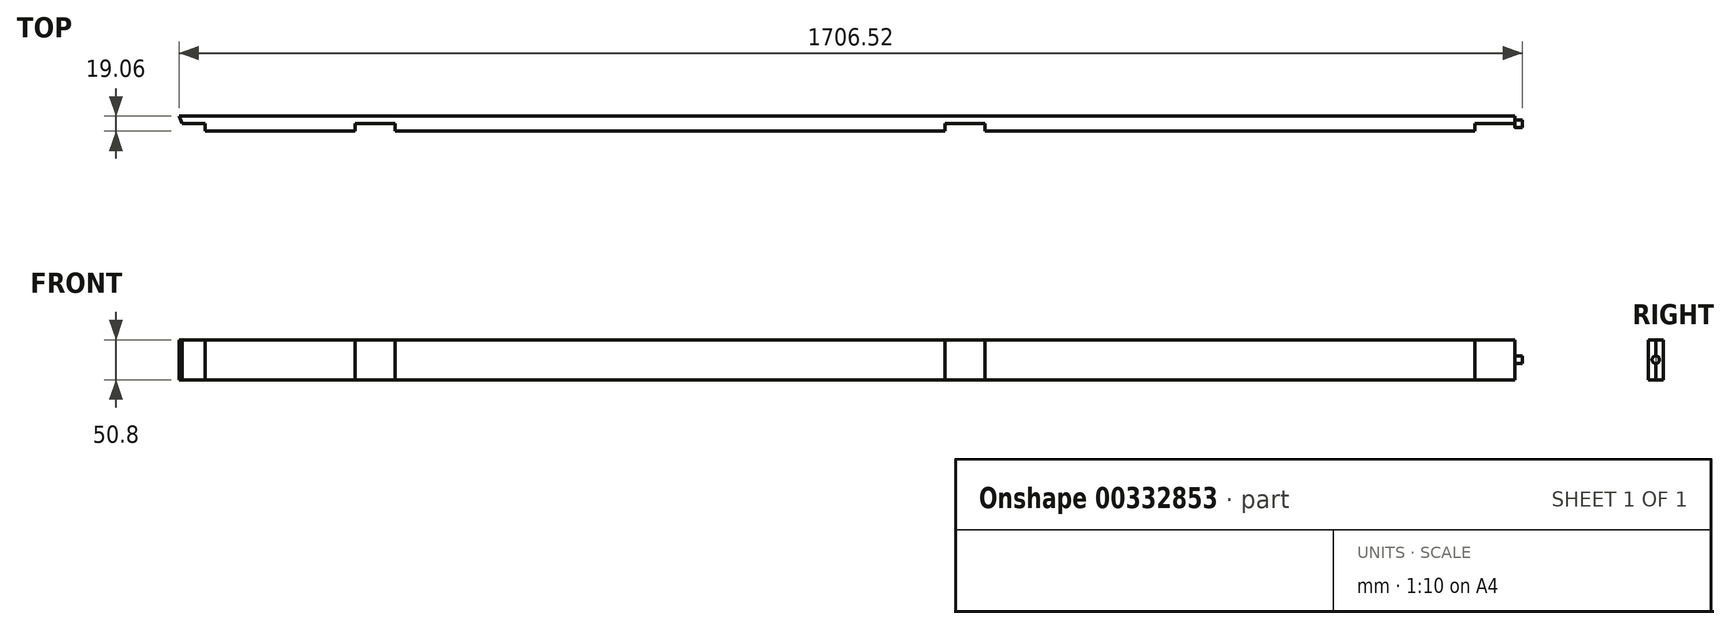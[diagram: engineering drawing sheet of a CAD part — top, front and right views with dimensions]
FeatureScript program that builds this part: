
annotation { "Feature Type Name" : "Feature", "Feature Type Description" : "" }
export const myFeature = defineFeature(function(context is Context, id is Id, definition is map)
    precondition{}
    {
        {
            var Q0;
            Q0=qCreatedBy(makeId("Top.planeOp"),FACE);
            var sketch = newSketch(context, id + "F0", { "sketchPlane" : qUnion([Q0])});
            skLineSegment(sketch, "E0.bottom", {"start": v(-1663.7, -9.52) * mm, "end": v(-1473.2, -9.52) * mm});
            skLineSegment(sketch, "E0.right", {"start": v(0, 0) * mm, "end": v(0, 9.53) * mm});
            skLineSegment(sketch, "E1", {"start": v(-1693.05, 0) * mm, "end": v(-1697, 9.52) * mm});
            skLineSegment(sketch, "E2", {"start": v(0, 9.53) * mm, "end": v(-1697, 9.52) * mm});
            skLineSegment(sketch, "E3.top", {"start": v(-1693.05, 0) * mm, "end": v(-1663.7, 0) * mm});
            skLineSegment(sketch, "E3.right", {"start": v(-1663.7, -9.52) * mm, "end": v(-1663.7, 0) * mm});
            skLineSegment(sketch, "E4.top", {"start": v(-1473.2, 0) * mm, "end": v(-1422.4, 0) * mm});
            skLineSegment(sketch, "E4.left", {"start": v(-1473.2, -9.52) * mm, "end": v(-1473.2, 0) * mm});
            skLineSegment(sketch, "E4.right", {"start": v(-1422.4, -9.52) * mm, "end": v(-1422.4, 0) * mm});
            skLineSegment(sketch, "E5.trimOffspring", {"start": v(-1422.4, -9.52) * mm, "end": v(-723.9, -9.52) * mm});
            skLineSegment(sketch, "E6.top", {"start": v(-723.9, 0) * mm, "end": v(-673.1, 0) * mm});
            skLineSegment(sketch, "E6.left", {"start": v(-723.9, -9.52) * mm, "end": v(-723.9, 0) * mm});
            skLineSegment(sketch, "E6.right", {"start": v(-673.1, -9.52) * mm, "end": v(-673.1, 0) * mm});
            skLineSegment(sketch, "E7.trimOffspring", {"start": v(-673.1, -9.52) * mm, "end": v(-50.8, -9.52) * mm});
            skLineSegment(sketch, "E8.top", {"start": v(-50.8, 0) * mm, "end": v(0, 0) * mm});
            skLineSegment(sketch, "E8.left", {"start": v(-50.8, -9.52) * mm, "end": v(-50.8, 0) * mm});
            skPoint(sketch, "E9.orphan", {"position": v(0, -9.52) * mm});
            skSolve(sketch);
        }
        {
            var Q0;
            Q0 = qSketchRegion(id + "F0", true);
            extrude(context, id + "F1", {"entities" : qUnion([Q0]), "endBound" : BoundingType.SYMMETRIC, "depth" : 50.8 * mm});
        }
        {
            var Q0;
            Q0=qCreatedBy(makeId("Right.planeOp"),FACE);
            var sketch = newSketch(context, id + "F2", { "sketchPlane" : qUnion([Q0])});
            skCircle(sketch, "E10", {"center": v(0, 0) * mm, "radius": 4.76 * mm});
            skSolve(sketch);
        }
        {
            var Q0;
            Q0 = qSketchRegion(id + "F2", true);
            extrude(context, id + "F3", {"entities" : qUnion([Q0]), "operationType" : NewBodyOperationType.ADD, "depth" : 9.52 * mm});
        }
    });
